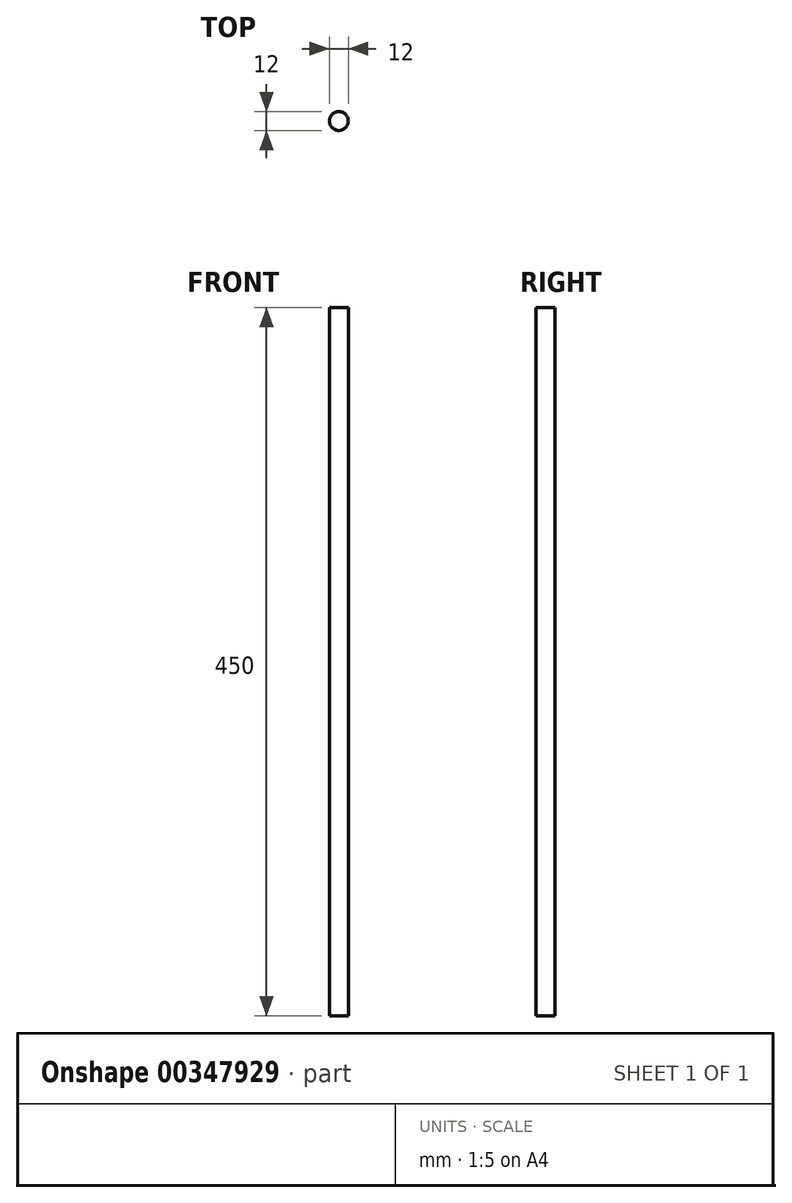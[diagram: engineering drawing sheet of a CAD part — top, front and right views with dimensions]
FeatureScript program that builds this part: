
annotation { "Feature Type Name" : "Feature", "Feature Type Description" : "" }
export const myFeature = defineFeature(function(context is Context, id is Id, definition is map)
    precondition{}
    {
        {
            var Q0;
            Q0=qCreatedBy(makeId("Top.planeOp"),FACE);
            var sketch = newSketch(context, id + "F0", { "sketchPlane" : qUnion([Q0])});
            skCircle(sketch, "E0", {"center": v(0, 0) * mm, "radius": 6 * mm});
            skSolve(sketch);
        }
        {
            var Q0;
            Q0=qSketchRegion(id+"F0",true);
            extrude(context, id + "F1", {"entities" : qUnion([Q0]), "depth" : 450 * mm});
        }
    });
